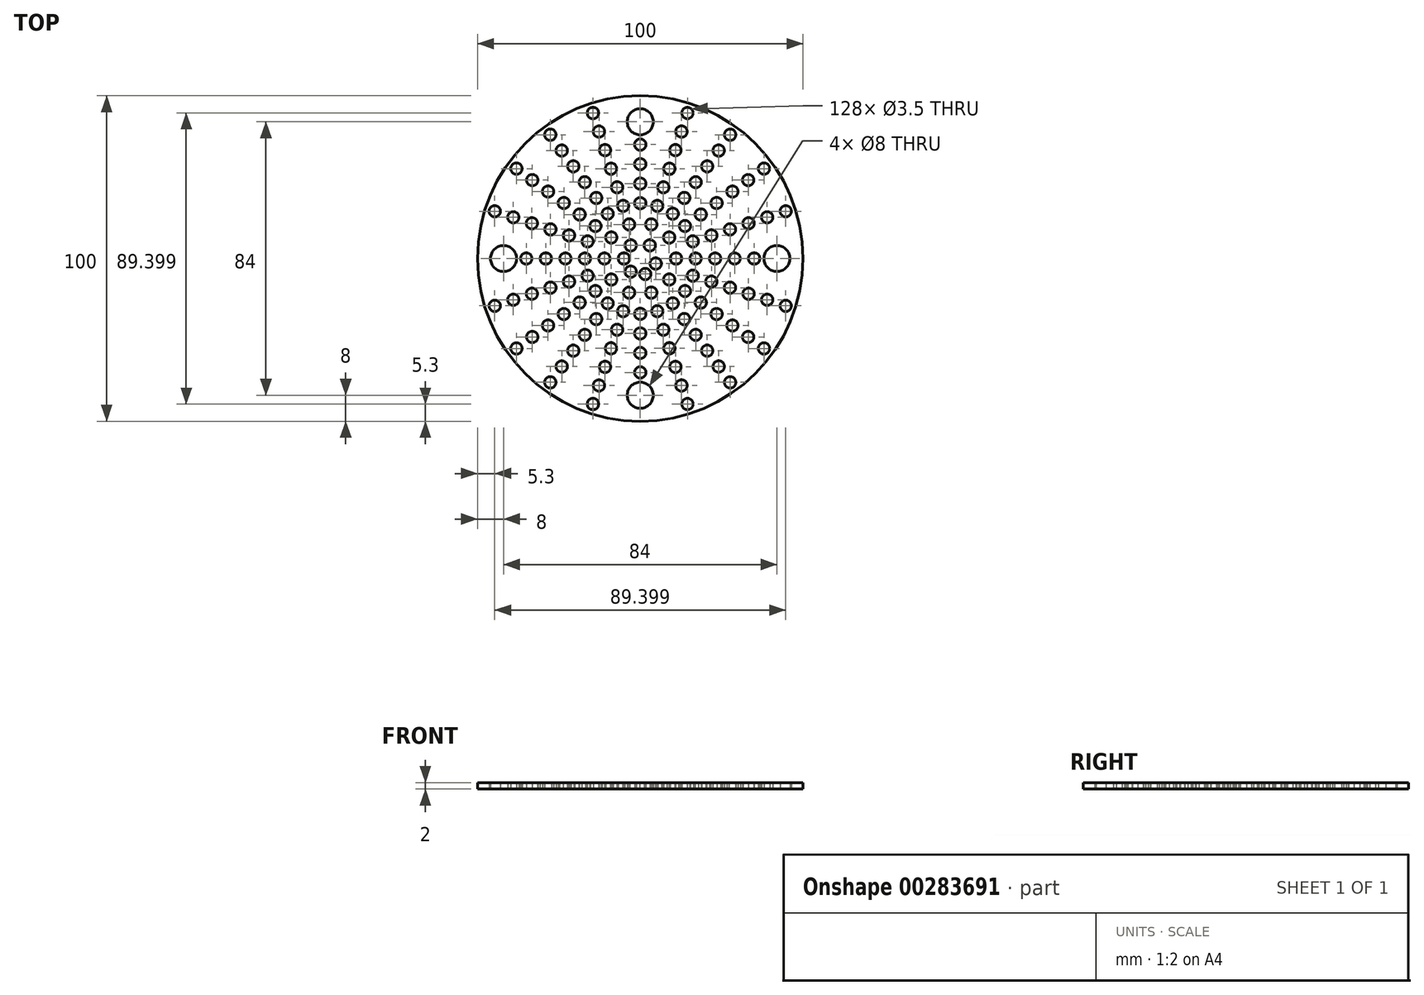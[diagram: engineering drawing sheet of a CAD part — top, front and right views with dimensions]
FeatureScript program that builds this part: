
annotation { "Feature Type Name" : "Feature", "Feature Type Description" : "" }
export const myFeature = defineFeature(function(context is Context, id is Id, definition is map)
    precondition{}
    {
        {
            var Q0;
            Q0=qCreatedBy(makeId("Top.planeOp"),FACE);
            var sketch = newSketch(context, id + "F0", { "sketchPlane" : qUnion([Q0])});
            skCircle(sketch, "E0", {"center": v(0, 0) * mm, "radius": 50 * mm});
            skCircle(sketch, "E1", {"center": v(0, 42) * mm, "radius": 4 * mm});
            skCircle(sketch, "E2.1.0", {"center": v(42, 0) * mm, "radius": 4 * mm});
            skCircle(sketch, "E2.2.0", {"center": v(0, -42) * mm, "radius": 4 * mm});
            skCircle(sketch, "E2.3.0", {"center": v(-42, 0) * mm, "radius": 4 * mm});
            skLineSegment(sketch, "E2.anchor1", {"start": v(0, 0) * mm, "end": v(0, 42) * mm, "construction": true});
            skLineSegment(sketch, "E2.anchor2", {"start": v(0, 0) * mm, "end": v(-42, 0) * mm, "construction": true});
            skCircle(sketch, "E3.1.0.0", {"center": v(11, 0) * mm, "radius": 1.75 * mm});
            skCircle(sketch, "E3.2.0.0", {"center": v(17, 0) * mm, "radius": 1.75 * mm});
            skCircle(sketch, "E3.3.0.0", {"center": v(23, 0) * mm, "radius": 1.75 * mm});
            skCircle(sketch, "E3.4.0.0", {"center": v(29, 0) * mm, "radius": 1.75 * mm});
            skCircle(sketch, "E3.5.0.0", {"center": v(35, 0) * mm, "radius": 1.75 * mm});
            skLineSegment(sketch, "E3.direction1", {"start": v(5, 0) * mm, "end": v(11, 0) * mm, "construction": true});
            skCircle(sketch, "E4.1.0", {"center": v(39, 12.67) * mm, "radius": 1.75 * mm});
            skCircle(sketch, "E4.1.1", {"center": v(33.29, 10.82) * mm, "radius": 1.75 * mm});
            skCircle(sketch, "E4.1.2", {"center": v(44.7, 14.52) * mm, "radius": 1.75 * mm});
            skCircle(sketch, "E4.1.3", {"center": v(27.58, 8.96) * mm, "radius": 1.75 * mm});
            skCircle(sketch, "E4.1.5", {"center": v(21.87, 7.1) * mm, "radius": 1.75 * mm});
            skCircle(sketch, "E4.1.6", {"center": v(16.17, 5.25) * mm, "radius": 1.75 * mm});
            skLineSegment(sketch, "E4.1.9", {"start": v(4.76, 1.55) * mm, "end": v(10.46, 3.4) * mm, "construction": true});
            skCircle(sketch, "E4.2.0", {"center": v(33.17, 24.1) * mm, "radius": 1.75 * mm});
            skCircle(sketch, "E4.2.1", {"center": v(28.32, 20.57) * mm, "radius": 1.75 * mm});
            skCircle(sketch, "E4.2.2", {"center": v(38.02, 27.63) * mm, "radius": 1.75 * mm});
            skCircle(sketch, "E4.2.3", {"center": v(23.46, 17.05) * mm, "radius": 1.75 * mm});
            skCircle(sketch, "E4.2.5", {"center": v(18.6, 13.52) * mm, "radius": 1.75 * mm});
            skCircle(sketch, "E4.2.6", {"center": v(13.75, 10) * mm, "radius": 1.75 * mm});
            skCircle(sketch, "E4.2.7", {"center": v(8.9, 6.47) * mm, "radius": 1.75 * mm});
            skLineSegment(sketch, "E4.2.9", {"start": v(4.05, 2.94) * mm, "end": v(8.9, 6.47) * mm, "construction": true});
            skCircle(sketch, "E4.3.0", {"center": v(24.1, 33.17) * mm, "radius": 1.75 * mm});
            skCircle(sketch, "E4.3.1", {"center": v(20.57, 28.32) * mm, "radius": 1.75 * mm});
            skCircle(sketch, "E4.3.2", {"center": v(27.63, 38.02) * mm, "radius": 1.75 * mm});
            skCircle(sketch, "E4.3.3", {"center": v(17.05, 23.46) * mm, "radius": 1.75 * mm});
            skCircle(sketch, "E4.3.5", {"center": v(13.52, 18.6) * mm, "radius": 1.75 * mm});
            skCircle(sketch, "E4.3.6", {"center": v(10, 13.75) * mm, "radius": 1.75 * mm});
            skCircle(sketch, "E4.3.8", {"center": v(2.94, 4.05) * mm, "radius": 1.75 * mm});
            skLineSegment(sketch, "E4.3.9", {"start": v(2.94, 4.05) * mm, "end": v(6.47, 8.9) * mm, "construction": true});
            skCircle(sketch, "E4.4.0", {"center": v(12.67, 39) * mm, "radius": 1.75 * mm});
            skCircle(sketch, "E4.4.1", {"center": v(10.82, 33.29) * mm, "radius": 1.75 * mm});
            skCircle(sketch, "E4.4.2", {"center": v(14.52, 44.7) * mm, "radius": 1.75 * mm});
            skCircle(sketch, "E4.4.3", {"center": v(8.96, 27.58) * mm, "radius": 1.75 * mm});
            skCircle(sketch, "E4.4.5", {"center": v(7.1, 21.87) * mm, "radius": 1.75 * mm});
            skCircle(sketch, "E4.4.6", {"center": v(5.25, 16.17) * mm, "radius": 1.75 * mm});
            skCircle(sketch, "E4.4.7", {"center": v(3.4, 10.46) * mm, "radius": 1.75 * mm});
            skLineSegment(sketch, "E4.4.9", {"start": v(1.55, 4.76) * mm, "end": v(3.4, 10.46) * mm, "construction": true});
            skCircle(sketch, "E4.5.1", {"center": v(0, 35) * mm, "radius": 1.75 * mm});
            skCircle(sketch, "E4.5.3", {"center": v(0, 29) * mm, "radius": 1.75 * mm});
            skCircle(sketch, "E4.5.5", {"center": v(0, 23) * mm, "radius": 1.75 * mm});
            skCircle(sketch, "E4.5.6", {"center": v(0, 17) * mm, "radius": 1.75 * mm});
            skLineSegment(sketch, "E4.5.9", {"start": v(0, 5) * mm, "end": v(0, 11) * mm, "construction": true});
            skCircle(sketch, "E4.6.0", {"center": v(-12.67, 39) * mm, "radius": 1.75 * mm});
            skCircle(sketch, "E4.6.1", {"center": v(-10.82, 33.29) * mm, "radius": 1.75 * mm});
            skCircle(sketch, "E4.6.2", {"center": v(-14.52, 44.7) * mm, "radius": 1.75 * mm});
            skCircle(sketch, "E4.6.3", {"center": v(-8.96, 27.58) * mm, "radius": 1.75 * mm});
            skCircle(sketch, "E4.6.5", {"center": v(-7.1, 21.87) * mm, "radius": 1.75 * mm});
            skCircle(sketch, "E4.6.6", {"center": v(-5.25, 16.17) * mm, "radius": 1.75 * mm});
            skCircle(sketch, "E4.6.7", {"center": v(-3.4, 10.46) * mm, "radius": 1.75 * mm});
            skLineSegment(sketch, "E4.6.9", {"start": v(-1.55, 4.76) * mm, "end": v(-3.4, 10.46) * mm, "construction": true});
            skCircle(sketch, "E4.7.0", {"center": v(-24.1, 33.17) * mm, "radius": 1.75 * mm});
            skCircle(sketch, "E4.7.1", {"center": v(-20.57, 28.32) * mm, "radius": 1.75 * mm});
            skCircle(sketch, "E4.7.2", {"center": v(-27.63, 38.02) * mm, "radius": 1.75 * mm});
            skCircle(sketch, "E4.7.3", {"center": v(-17.05, 23.46) * mm, "radius": 1.75 * mm});
            skCircle(sketch, "E4.7.5", {"center": v(-13.52, 18.6) * mm, "radius": 1.75 * mm});
            skCircle(sketch, "E4.7.6", {"center": v(-10, 13.75) * mm, "radius": 1.75 * mm});
            skCircle(sketch, "E4.7.8", {"center": v(-2.94, 4.05) * mm, "radius": 1.75 * mm});
            skLineSegment(sketch, "E4.7.9", {"start": v(-2.94, 4.05) * mm, "end": v(-6.47, 8.9) * mm, "construction": true});
            skCircle(sketch, "E4.8.0", {"center": v(-33.17, 24.1) * mm, "radius": 1.75 * mm});
            skCircle(sketch, "E4.8.1", {"center": v(-28.32, 20.57) * mm, "radius": 1.75 * mm});
            skCircle(sketch, "E4.8.2", {"center": v(-38.02, 27.63) * mm, "radius": 1.75 * mm});
            skCircle(sketch, "E4.8.3", {"center": v(-23.46, 17.05) * mm, "radius": 1.75 * mm});
            skCircle(sketch, "E4.8.5", {"center": v(-18.6, 13.52) * mm, "radius": 1.75 * mm});
            skCircle(sketch, "E4.8.6", {"center": v(-13.75, 10) * mm, "radius": 1.75 * mm});
            skCircle(sketch, "E4.8.7", {"center": v(-8.9, 6.47) * mm, "radius": 1.75 * mm});
            skLineSegment(sketch, "E4.8.9", {"start": v(-4.05, 2.94) * mm, "end": v(-8.9, 6.47) * mm, "construction": true});
            skCircle(sketch, "E4.9.0", {"center": v(-39, 12.67) * mm, "radius": 1.75 * mm});
            skCircle(sketch, "E4.9.1", {"center": v(-33.29, 10.82) * mm, "radius": 1.75 * mm});
            skCircle(sketch, "E4.9.2", {"center": v(-44.7, 14.52) * mm, "radius": 1.75 * mm});
            skCircle(sketch, "E4.9.3", {"center": v(-27.58, 8.96) * mm, "radius": 1.75 * mm});
            skCircle(sketch, "E4.9.5", {"center": v(-21.87, 7.1) * mm, "radius": 1.75 * mm});
            skCircle(sketch, "E4.9.6", {"center": v(-16.17, 5.25) * mm, "radius": 1.75 * mm});
            skLineSegment(sketch, "E4.9.9", {"start": v(-4.76, 1.55) * mm, "end": v(-10.46, 3.4) * mm, "construction": true});
            skCircle(sketch, "E4.10.1", {"center": v(-35, 0) * mm, "radius": 1.75 * mm});
            skCircle(sketch, "E4.10.3", {"center": v(-29, 0) * mm, "radius": 1.75 * mm});
            skCircle(sketch, "E4.10.5", {"center": v(-23, 0) * mm, "radius": 1.75 * mm});
            skCircle(sketch, "E4.10.6", {"center": v(-17, 0) * mm, "radius": 1.75 * mm});
            skCircle(sketch, "E4.10.7", {"center": v(-11, 0) * mm, "radius": 1.75 * mm});
            skCircle(sketch, "E4.10.8", {"center": v(-5, 0) * mm, "radius": 1.75 * mm});
            skLineSegment(sketch, "E4.10.9", {"start": v(-5, 0) * mm, "end": v(-11, 0) * mm, "construction": true});
            skCircle(sketch, "E4.11.0", {"center": v(-39, -12.67) * mm, "radius": 1.75 * mm});
            skCircle(sketch, "E4.11.1", {"center": v(-33.29, -10.82) * mm, "radius": 1.75 * mm});
            skCircle(sketch, "E4.11.2", {"center": v(-44.7, -14.52) * mm, "radius": 1.75 * mm});
            skCircle(sketch, "E4.11.3", {"center": v(-27.58, -8.96) * mm, "radius": 1.75 * mm});
            skCircle(sketch, "E4.11.5", {"center": v(-21.87, -7.1) * mm, "radius": 1.75 * mm});
            skCircle(sketch, "E4.11.6", {"center": v(-16.17, -5.25) * mm, "radius": 1.75 * mm});
            skLineSegment(sketch, "E4.11.9", {"start": v(-4.76, -1.55) * mm, "end": v(-10.46, -3.4) * mm, "construction": true});
            skCircle(sketch, "E4.12.0", {"center": v(-33.17, -24.1) * mm, "radius": 1.75 * mm});
            skCircle(sketch, "E4.12.1", {"center": v(-28.32, -20.57) * mm, "radius": 1.75 * mm});
            skCircle(sketch, "E4.12.2", {"center": v(-38.02, -27.63) * mm, "radius": 1.75 * mm});
            skCircle(sketch, "E4.12.3", {"center": v(-23.46, -17.05) * mm, "radius": 1.75 * mm});
            skCircle(sketch, "E4.12.5", {"center": v(-18.6, -13.52) * mm, "radius": 1.75 * mm});
            skCircle(sketch, "E4.12.6", {"center": v(-13.75, -10) * mm, "radius": 1.75 * mm});
            skCircle(sketch, "E4.12.7", {"center": v(-8.9, -6.47) * mm, "radius": 1.75 * mm});
            skLineSegment(sketch, "E4.12.9", {"start": v(-4.05, -2.94) * mm, "end": v(-8.9, -6.47) * mm, "construction": true});
            skCircle(sketch, "E4.13.0", {"center": v(-24.1, -33.17) * mm, "radius": 1.75 * mm});
            skCircle(sketch, "E4.13.1", {"center": v(-20.57, -28.32) * mm, "radius": 1.75 * mm});
            skCircle(sketch, "E4.13.2", {"center": v(-27.63, -38.02) * mm, "radius": 1.75 * mm});
            skCircle(sketch, "E4.13.3", {"center": v(-17.05, -23.46) * mm, "radius": 1.75 * mm});
            skCircle(sketch, "E4.13.5", {"center": v(-13.52, -18.6) * mm, "radius": 1.75 * mm});
            skCircle(sketch, "E4.13.6", {"center": v(-10, -13.75) * mm, "radius": 1.75 * mm});
            skCircle(sketch, "E4.13.8", {"center": v(-2.94, -4.05) * mm, "radius": 1.75 * mm});
            skLineSegment(sketch, "E4.13.9", {"start": v(-2.94, -4.05) * mm, "end": v(-6.47, -8.9) * mm, "construction": true});
            skCircle(sketch, "E4.14.0", {"center": v(-12.67, -39) * mm, "radius": 1.75 * mm});
            skCircle(sketch, "E4.14.1", {"center": v(-10.82, -33.29) * mm, "radius": 1.75 * mm});
            skCircle(sketch, "E4.14.2", {"center": v(-14.52, -44.7) * mm, "radius": 1.75 * mm});
            skCircle(sketch, "E4.14.3", {"center": v(-8.96, -27.58) * mm, "radius": 1.75 * mm});
            skCircle(sketch, "E4.14.5", {"center": v(-7.1, -21.87) * mm, "radius": 1.75 * mm});
            skCircle(sketch, "E4.14.6", {"center": v(-5.25, -16.17) * mm, "radius": 1.75 * mm});
            skCircle(sketch, "E4.14.7", {"center": v(-3.4, -10.46) * mm, "radius": 1.75 * mm});
            skLineSegment(sketch, "E4.14.9", {"start": v(-1.55, -4.76) * mm, "end": v(-3.4, -10.46) * mm, "construction": true});
            skCircle(sketch, "E4.15.1", {"center": v(0, -35) * mm, "radius": 1.75 * mm});
            skCircle(sketch, "E4.15.3", {"center": v(0, -29) * mm, "radius": 1.75 * mm});
            skCircle(sketch, "E4.15.5", {"center": v(0, -23) * mm, "radius": 1.75 * mm});
            skCircle(sketch, "E4.15.6", {"center": v(0, -17) * mm, "radius": 1.75 * mm});
            skLineSegment(sketch, "E4.15.9", {"start": v(0, -5) * mm, "end": v(0, -11) * mm, "construction": true});
            skCircle(sketch, "E4.16.0", {"center": v(12.67, -39) * mm, "radius": 1.75 * mm});
            skCircle(sketch, "E4.16.1", {"center": v(10.82, -33.29) * mm, "radius": 1.75 * mm});
            skCircle(sketch, "E4.16.2", {"center": v(14.52, -44.7) * mm, "radius": 1.75 * mm});
            skCircle(sketch, "E4.16.3", {"center": v(8.96, -27.58) * mm, "radius": 1.75 * mm});
            skCircle(sketch, "E4.16.5", {"center": v(7.1, -21.87) * mm, "radius": 1.75 * mm});
            skCircle(sketch, "E4.16.6", {"center": v(5.25, -16.17) * mm, "radius": 1.75 * mm});
            skCircle(sketch, "E4.16.7", {"center": v(3.4, -10.46) * mm, "radius": 1.75 * mm});
            skCircle(sketch, "E4.16.8", {"center": v(1.55, -4.76) * mm, "radius": 1.75 * mm});
            skLineSegment(sketch, "E4.16.9", {"start": v(1.55, -4.76) * mm, "end": v(3.4, -10.46) * mm, "construction": true});
            skCircle(sketch, "E4.17.0", {"center": v(24.1, -33.17) * mm, "radius": 1.75 * mm});
            skCircle(sketch, "E4.17.1", {"center": v(20.57, -28.32) * mm, "radius": 1.75 * mm});
            skCircle(sketch, "E4.17.2", {"center": v(27.63, -38.02) * mm, "radius": 1.75 * mm});
            skCircle(sketch, "E4.17.3", {"center": v(17.05, -23.46) * mm, "radius": 1.75 * mm});
            skCircle(sketch, "E4.17.5", {"center": v(13.52, -18.6) * mm, "radius": 1.75 * mm});
            skCircle(sketch, "E4.17.6", {"center": v(10, -13.75) * mm, "radius": 1.75 * mm});
            skLineSegment(sketch, "E4.17.9", {"start": v(2.94, -4.05) * mm, "end": v(6.47, -8.9) * mm, "construction": true});
            skCircle(sketch, "E4.18.0", {"center": v(33.17, -24.1) * mm, "radius": 1.75 * mm});
            skCircle(sketch, "E4.18.1", {"center": v(28.32, -20.57) * mm, "radius": 1.75 * mm});
            skCircle(sketch, "E4.18.2", {"center": v(38.02, -27.63) * mm, "radius": 1.75 * mm});
            skCircle(sketch, "E4.18.3", {"center": v(23.46, -17.05) * mm, "radius": 1.75 * mm});
            skCircle(sketch, "E4.18.5", {"center": v(18.6, -13.52) * mm, "radius": 1.75 * mm});
            skCircle(sketch, "E4.18.6", {"center": v(13.75, -10) * mm, "radius": 1.75 * mm});
            skCircle(sketch, "E4.18.7", {"center": v(8.9, -6.47) * mm, "radius": 1.75 * mm});
            skLineSegment(sketch, "E4.18.9", {"start": v(4.05, -2.94) * mm, "end": v(8.9, -6.47) * mm, "construction": true});
            skCircle(sketch, "E4.19.0", {"center": v(39, -12.67) * mm, "radius": 1.75 * mm});
            skCircle(sketch, "E4.19.1", {"center": v(33.29, -10.82) * mm, "radius": 1.75 * mm});
            skCircle(sketch, "E4.19.2", {"center": v(44.7, -14.52) * mm, "radius": 1.75 * mm});
            skCircle(sketch, "E4.19.3", {"center": v(27.58, -8.96) * mm, "radius": 1.75 * mm});
            skCircle(sketch, "E4.19.5", {"center": v(21.87, -7.1) * mm, "radius": 1.75 * mm});
            skCircle(sketch, "E4.19.6", {"center": v(16.17, -5.25) * mm, "radius": 1.75 * mm});
            skCircle(sketch, "E4.19.8", {"center": v(4.76, -1.55) * mm, "radius": 1.75 * mm});
            skLineSegment(sketch, "E4.19.9", {"start": v(4.76, -1.55) * mm, "end": v(10.46, -3.4) * mm, "construction": true});
            skSolve(sketch);
        }
        {
            var Q0;
            Q0 = qSketchRegion(id + "F0", true);
            extrude(context, id + "F1", {"entities" : qUnion([Q0]), "depth" : 2 * mm});
        }
    });
